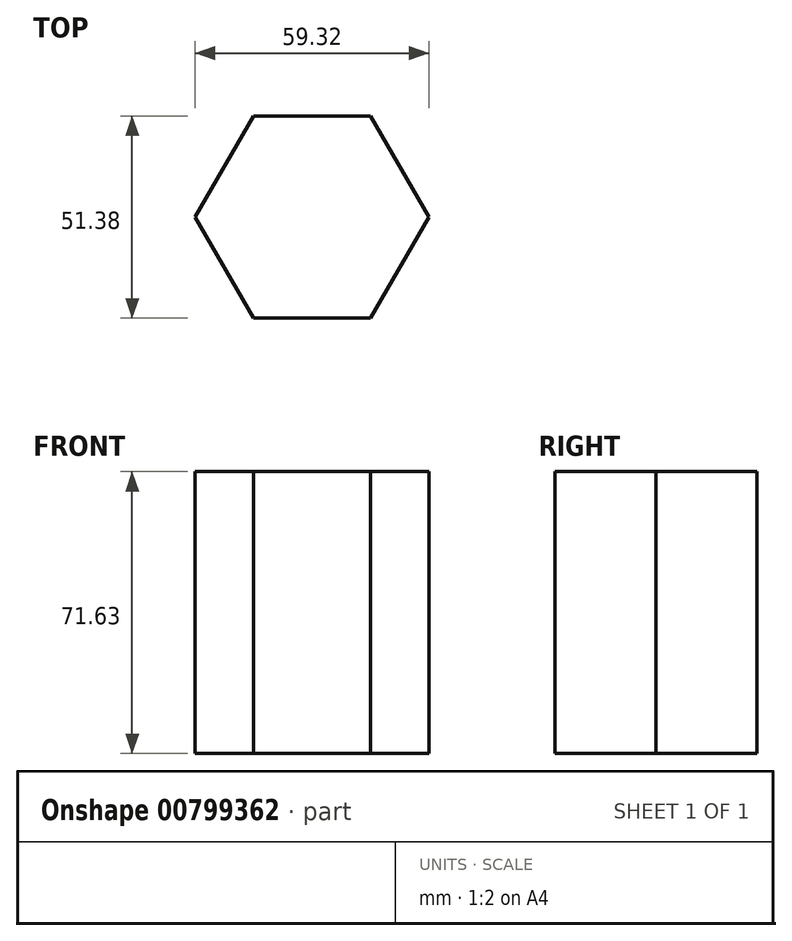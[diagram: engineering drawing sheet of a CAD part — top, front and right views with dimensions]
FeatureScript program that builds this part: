
annotation { "Feature Type Name" : "Feature", "Feature Type Description" : "" }
export const myFeature = defineFeature(function(context is Context, id is Id, definition is map)
    precondition{}
    {
        {
            var Q0;
            Q0=qCreatedBy(makeId("Top.planeOp"),FACE);
            var sketch = newSketch(context, id + "F0", { "sketchPlane" : qUnion([Q0])});
            skCircle(sketch, "E0.cCircle", {"center": v(0, 0) * mm, "radius": 25.69 * mm, "construction": true});
            skLineSegment(sketch, "E0.0", {"start": v(29.66, 0) * mm, "end": v(14.83, -25.69) * mm});
            skLineSegment(sketch, "E0.1", {"start": v(14.83, -25.69) * mm, "end": v(-14.83, -25.68) * mm});
            skLineSegment(sketch, "E0.2", {"start": v(-14.83, -25.68) * mm, "end": v(-29.66, 0) * mm});
            skLineSegment(sketch, "E0.3", {"start": v(-29.66, 0) * mm, "end": v(-14.83, 25.69) * mm});
            skLineSegment(sketch, "E0.4", {"start": v(-14.83, 25.69) * mm, "end": v(14.83, 25.68) * mm});
            skLineSegment(sketch, "E0.5", {"start": v(14.83, 25.68) * mm, "end": v(29.66, 0) * mm});
            skPoint(sketch, "E0.0.midPoint", {"position": v(22.24, -12.85) * mm});
            skSolve(sketch);
        }
        {
            var Q0;
            Q0=makeQuery(id+"F0.imprint","IMPRINT",FACE,{"disambiguationData":[TD([[makeQuery(id+"F0.imprint","IMPRINT",EDGE,{"derivedFrom":sQuery(id+"F0.wireOp",EDGE,"E0.0")}),-1.0]])]});
            extrude(context, id + "F1", {"entities" : qUnion([Q0]), "depth" : 46.23 * mm, "offsetDistance" : 25.4 * mm});
        }
        {
            var Q0;
            Q0=makeQuery(id+"F1.opExtrude","CAP_FACE",FACE,{"disambiguationData":[OSD([sQuery(id+"F0.wireOp",EDGE,"E0.0"),sQuery(id+"F0.wireOp",EDGE,"E0.1"),sQuery(id+"F0.wireOp",EDGE,"E0.2"),sQuery(id+"F0.wireOp",EDGE,"E0.3"),sQuery(id+"F0.wireOp",EDGE,"E0.4"),sQuery(id+"F0.wireOp",EDGE,"E0.5")])],"isStart":false});
            extrude(context, id + "F2", {"entities" : qUnion([Q0]), "operationType" : NewBodyOperationType.ADD, "depth" : 25.4 * mm, "offsetDistance" : 25.4 * mm});
        }
    });
